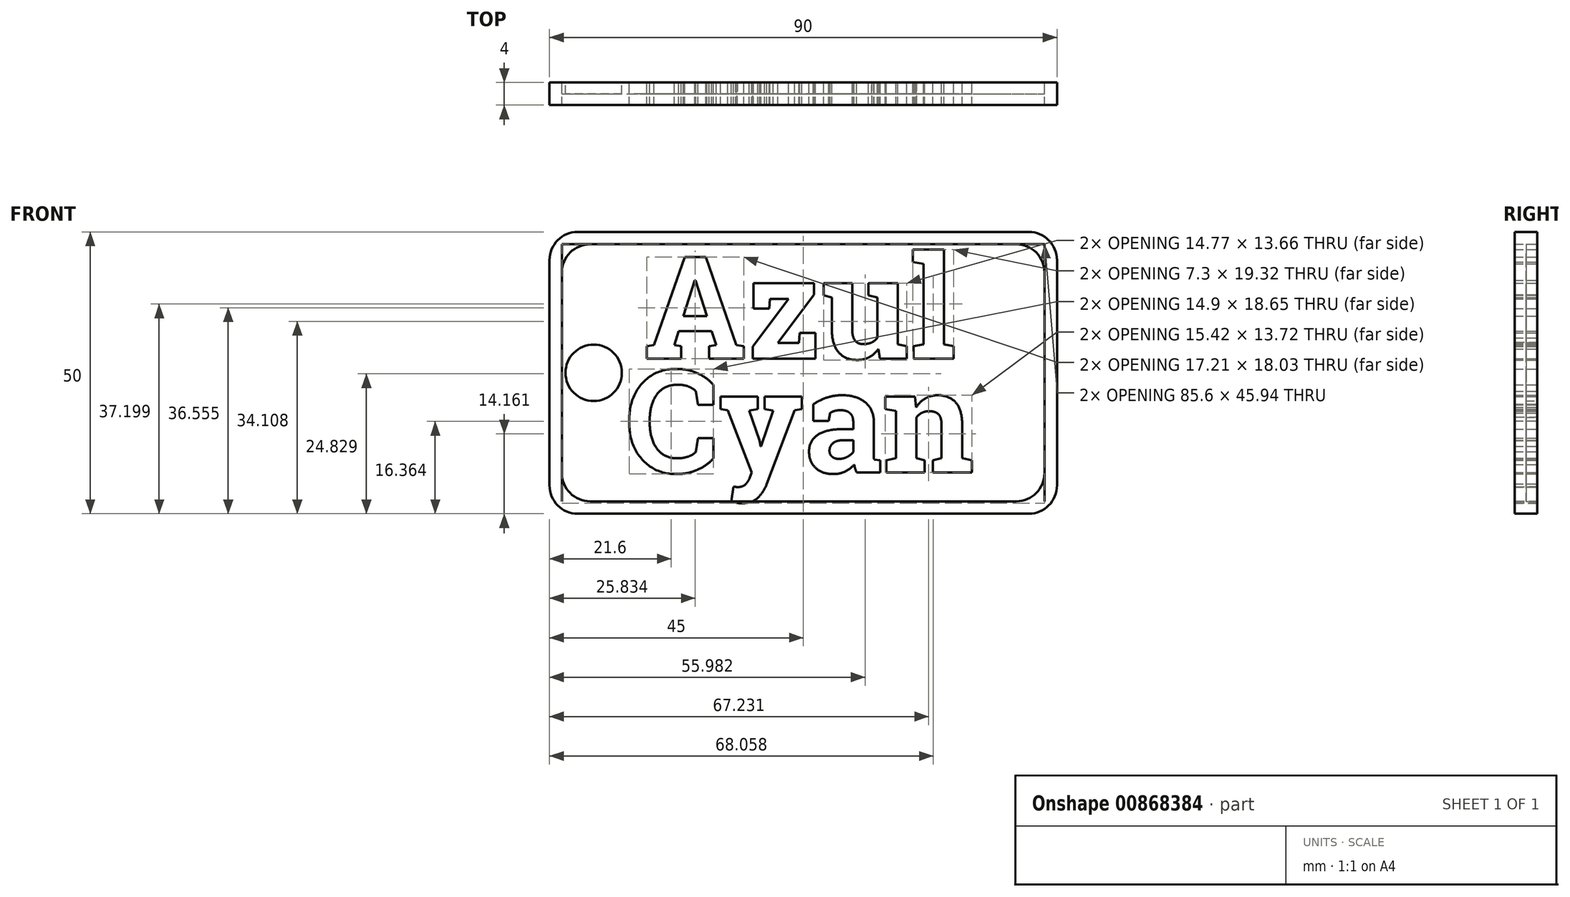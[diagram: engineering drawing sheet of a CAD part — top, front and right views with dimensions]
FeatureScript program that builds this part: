
annotation { "Feature Type Name" : "Feature", "Feature Type Description" : "" }
export const myFeature = defineFeature(function(context is Context, id is Id, definition is map)
    precondition{}
    {
        {
            var Q0;
            Q0=qCreatedBy(makeId("Front.planeOp"),FACE);
            var sketch = newSketch(context, id + "F0", { "sketchPlane" : qUnion([Q0])});
            skLineSegment(sketch, "E0.bottom", {"start": v(-45, 25) * mm, "end": v(45, 25) * mm});
            skLineSegment(sketch, "E0.top", {"start": v(-45, -25) * mm, "end": v(45, -25) * mm});
            skLineSegment(sketch, "E0.left", {"start": v(-45, 25) * mm, "end": v(-45, -25) * mm});
            skLineSegment(sketch, "E0.right", {"start": v(45, 25) * mm, "end": v(45, -25) * mm});
            skLineSegment(sketch, "E1.0", {"start": v(-42.8, 22.8) * mm, "end": v(42.8, 22.8) * mm});
            skLineSegment(sketch, "E1.1", {"start": v(-42.8, 22.8) * mm, "end": v(-42.8, -22.8) * mm});
            skLineSegment(sketch, "E1.2", {"start": v(-42.8, -22.8) * mm, "end": v(42.8, -22.8) * mm});
            skLineSegment(sketch, "E1.3", {"start": v(42.8, 22.8) * mm, "end": v(42.8, -22.8) * mm});
            skCircle(sketch, "E2", {"center": v(-37.16, 0) * mm, "radius": 5 * mm});
            skText(sketch, "E3", { "text": "Azul", "fontName": "RobotoSlab-Bold.ttf"});
            skText(sketch, "E4", { "text": "Cyan", "fontName": "RobotoSlab-Bold.ttf"});
            const initialGuessF0  = {"E3": [-0.02828, 0.00254, 1, 0, 0.01826], "E4": [-0.0315, -0.0177, 1, 0, 0.01836]};
            skSetInitialGuess(sketch, initialGuessF0);
            skSolve(sketch);
        }
        {
            var Q0;
            Q0=makeQuery(id+"F0.imprint","IMPRINT",FACE,{"disambiguationData":[TD([[makeQuery(id+"F0.imprint","IMPRINT",EDGE,{"derivedFrom":sQuery(id+"F0.wireOp",EDGE,"ed1831c7-6287-4320-802f-d40747e157da.sketch_text.stroke-16")}),1.0]])]});
            var Q1;
            Q1=makeQuery(id+"F0.imprint","IMPRINT",FACE,{"disambiguationData":[TD([[makeQuery(id+"F0.imprint","IMPRINT",EDGE,{"derivedFrom":sQuery(id+"F0.wireOp",EDGE,"ed1831c7-6287-4320-802f-d40747e157da.sketch_text.stroke-90")}),1.0]])]});
            var Q2;
            Q2=makeQuery(id+"F0.imprint","IMPRINT",FACE,{"disambiguationData":[TD([[makeQuery(id+"F0.imprint","IMPRINT",EDGE,{"derivedFrom":sQuery(id+"F0.wireOp",EDGE,"ed1831c7-6287-4320-802f-d40747e157da.sketch_text.stroke-161")}),1.0]])]});
            var Q3;
            Q3=makeQuery(id+"F0.imprint","IMPRINT",FACE,{"disambiguationData":[TD([[makeQuery(id+"F0.imprint","IMPRINT",EDGE,{"derivedFrom":sQuery(id+"F0.wireOp",EDGE,"ed1831c7-6287-4320-802f-d40747e157da.sketch_text.stroke-281")}),1.0]])]});
            var Q4;
            Q4=makeQuery(id+"F0.imprint","IMPRINT",FACE,{"disambiguationData":[TD([[makeQuery(id+"F0.imprint","IMPRINT",EDGE,{"derivedFrom":sQuery(id+"F0.wireOp",EDGE,"ed1831c7-6287-4320-802f-d40747e157da.sketch_text.stroke-244")}),1.0]])]});
            var Q5;
            Q5=makeQuery(id+"F0.imprint","IMPRINT",FACE,{"disambiguationData":[TD([[makeQuery(id+"F0.imprint","IMPRINT",EDGE,{"derivedFrom":sQuery(id+"F0.wireOp",EDGE,"ed1831c7-6287-4320-802f-d40747e157da.sketch_text.stroke-218")}),1.0]])]});
            var Q6;
            Q6=makeQuery(id+"F0.imprint","IMPRINT",FACE,{"disambiguationData":[TD([[makeQuery(id+"F0.imprint","IMPRINT",EDGE,{"derivedFrom":sQuery(id+"F0.wireOp",EDGE,"E1.0")}),-1.0]])]});
            var Q7;
            Q7=makeQuery(id+"F0.imprint","IMPRINT",FACE,{"disambiguationData":[TD([[makeQuery(id+"F0.imprint","IMPRINT",EDGE,{"derivedFrom":sQuery(id+"F0.wireOp",EDGE,"E3.sketch_text.stroke-16")}),1.0]])]});
            var Q8;
            Q8=makeQuery(id+"F0.imprint","IMPRINT",FACE,{"disambiguationData":[TD([[makeQuery(id+"F0.imprint","IMPRINT",EDGE,{"derivedFrom":sQuery(id+"F0.wireOp",EDGE,"E4.sketch_text.stroke-77")}),1.0]])]});
            extrude(context, id + "F1", {"entities" : qUnion([Q0, Q1, Q2, Q3, Q4, Q5, Q6, Q7, Q8]), "depth" : 2 * mm, "offsetDistance" : 25 * mm});
        }
        {
            var Q0;
            Q0=makeQuery(id+"F0.imprint","IMPRINT",FACE,{"disambiguationData":[TD([[makeQuery(id+"F0.imprint","IMPRINT",EDGE,{"derivedFrom":sQuery(id+"F0.wireOp",EDGE,"ed1831c7-6287-4320-802f-d40747e157da.sketch_text.stroke-0")}),-1.0]])]});
            var Q1;
            Q1=makeQuery(id+"F0.imprint","IMPRINT",FACE,{"disambiguationData":[TD([[makeQuery(id+"F0.imprint","IMPRINT",EDGE,{"derivedFrom":sQuery(id+"F0.wireOp",EDGE,"ed1831c7-6287-4320-802f-d40747e157da.sketch_text.stroke-20")}),-1.0]])]});
            var Q2;
            Q2=makeQuery(id+"F0.imprint","IMPRINT",FACE,{"disambiguationData":[TD([[makeQuery(id+"F0.imprint","IMPRINT",EDGE,{"derivedFrom":sQuery(id+"F0.wireOp",EDGE,"ed1831c7-6287-4320-802f-d40747e157da.sketch_text.stroke-63")}),-1.0]])]});
            var Q3;
            Q3=makeQuery(id+"F0.imprint","IMPRINT",FACE,{"disambiguationData":[TD([[makeQuery(id+"F0.imprint","IMPRINT",EDGE,{"derivedFrom":sQuery(id+"F0.wireOp",EDGE,"ed1831c7-6287-4320-802f-d40747e157da.sketch_text.stroke-98")}),-1.0]])]});
            var Q4;
            Q4=makeQuery(id+"F0.imprint","IMPRINT",FACE,{"disambiguationData":[TD([[makeQuery(id+"F0.imprint","IMPRINT",EDGE,{"derivedFrom":sQuery(id+"F0.wireOp",EDGE,"ed1831c7-6287-4320-802f-d40747e157da.sketch_text.stroke-117")}),-1.0]])]});
            var Q5;
            Q5=makeQuery(id+"F0.imprint","IMPRINT",FACE,{"disambiguationData":[TD([[makeQuery(id+"F0.imprint","IMPRINT",EDGE,{"derivedFrom":sQuery(id+"F0.wireOp",EDGE,"ed1831c7-6287-4320-802f-d40747e157da.sketch_text.stroke-127")}),-1.0]])]});
            var Q6;
            Q6=makeQuery(id+"F0.imprint","IMPRINT",FACE,{"disambiguationData":[TD([[makeQuery(id+"F0.imprint","IMPRINT",EDGE,{"derivedFrom":sQuery(id+"F0.wireOp",EDGE,"ed1831c7-6287-4320-802f-d40747e157da.sketch_text.stroke-131")}),-1.0]])]});
            var Q7;
            Q7=makeQuery(id+"F0.imprint","IMPRINT",FACE,{"disambiguationData":[TD([[makeQuery(id+"F0.imprint","IMPRINT",EDGE,{"derivedFrom":sQuery(id+"F0.wireOp",EDGE,"ed1831c7-6287-4320-802f-d40747e157da.sketch_text.stroke-141")}),-1.0]])]});
            var Q8;
            Q8=makeQuery(id+"F0.imprint","IMPRINT",FACE,{"disambiguationData":[TD([[makeQuery(id+"F0.imprint","IMPRINT",EDGE,{"derivedFrom":sQuery(id+"F0.wireOp",EDGE,"ed1831c7-6287-4320-802f-d40747e157da.sketch_text.stroke-151")}),-1.0]])]});
            var Q9;
            Q9=makeQuery(id+"F0.imprint","IMPRINT",FACE,{"disambiguationData":[TD([[makeQuery(id+"F0.imprint","IMPRINT",EDGE,{"derivedFrom":sQuery(id+"F0.wireOp",EDGE,"ed1831c7-6287-4320-802f-d40747e157da.sketch_text.stroke-254")}),-1.0]])]});
            var Q10;
            Q10=makeQuery(id+"F0.imprint","IMPRINT",FACE,{"disambiguationData":[TD([[makeQuery(id+"F0.imprint","IMPRINT",EDGE,{"derivedFrom":sQuery(id+"F0.wireOp",EDGE,"ed1831c7-6287-4320-802f-d40747e157da.sketch_text.stroke-225")}),-1.0]])]});
            var Q11;
            Q11=makeQuery(id+"F0.imprint","IMPRINT",FACE,{"disambiguationData":[TD([[makeQuery(id+"F0.imprint","IMPRINT",EDGE,{"derivedFrom":sQuery(id+"F0.wireOp",EDGE,"ed1831c7-6287-4320-802f-d40747e157da.sketch_text.stroke-201")}),-1.0]])]});
            var Q12;
            Q12=makeQuery(id+"F0.imprint","IMPRINT",FACE,{"disambiguationData":[TD([[makeQuery(id+"F0.imprint","IMPRINT",EDGE,{"derivedFrom":sQuery(id+"F0.wireOp",EDGE,"ed1831c7-6287-4320-802f-d40747e157da.sketch_text.stroke-171")}),-1.0]])]});
            var Q13;
            Q13=makeQuery(id+"F0.imprint","IMPRINT",FACE,{"disambiguationData":[TD([[makeQuery(id+"F0.imprint","IMPRINT",EDGE,{"derivedFrom":sQuery(id+"F0.wireOp",EDGE,"E0.bottom")}),-1.0]])]});
            var Q14;
            Q14=makeQuery(id+"F0.imprint","IMPRINT",FACE,{"disambiguationData":[TD([[makeQuery(id+"F0.imprint","IMPRINT",EDGE,{"derivedFrom":sQuery(id+"F0.wireOp",EDGE,"E3.sketch_text.stroke-0")}),-1.0]])]});
            var Q15;
            Q15=makeQuery(id+"F0.imprint","IMPRINT",FACE,{"disambiguationData":[TD([[makeQuery(id+"F0.imprint","IMPRINT",EDGE,{"derivedFrom":sQuery(id+"F0.wireOp",EDGE,"E3.sketch_text.stroke-20")}),-1.0]])]});
            var Q16;
            Q16=makeQuery(id+"F0.imprint","IMPRINT",FACE,{"disambiguationData":[TD([[makeQuery(id+"F0.imprint","IMPRINT",EDGE,{"derivedFrom":sQuery(id+"F0.wireOp",EDGE,"E3.sketch_text.stroke-34")}),-1.0]])]});
            var Q17;
            Q17=makeQuery(id+"F0.imprint","IMPRINT",FACE,{"disambiguationData":[TD([[makeQuery(id+"F0.imprint","IMPRINT",EDGE,{"derivedFrom":sQuery(id+"F0.wireOp",EDGE,"E3.sketch_text.stroke-58")}),-1.0]])]});
            var Q18;
            Q18=makeQuery(id+"F0.imprint","IMPRINT",FACE,{"disambiguationData":[TD([[makeQuery(id+"F0.imprint","IMPRINT",EDGE,{"derivedFrom":sQuery(id+"F0.wireOp",EDGE,"E4.sketch_text.stroke-85")}),-1.0]])]});
            var Q19;
            Q19=makeQuery(id+"F0.imprint","IMPRINT",FACE,{"disambiguationData":[TD([[makeQuery(id+"F0.imprint","IMPRINT",EDGE,{"derivedFrom":sQuery(id+"F0.wireOp",EDGE,"E4.sketch_text.stroke-50")}),-1.0]])]});
            var Q20;
            Q20=makeQuery(id+"F0.imprint","IMPRINT",FACE,{"disambiguationData":[TD([[makeQuery(id+"F0.imprint","IMPRINT",EDGE,{"derivedFrom":sQuery(id+"F0.wireOp",EDGE,"E4.sketch_text.stroke-24")}),-1.0]])]});
            var Q21;
            Q21=makeQuery(id+"F0.imprint","IMPRINT",FACE,{"disambiguationData":[TD([[makeQuery(id+"F0.imprint","IMPRINT",EDGE,{"derivedFrom":sQuery(id+"F0.wireOp",EDGE,"E4.sketch_text.stroke-0")}),-1.0]])]});
            extrude(context, id + "F2", {"entities" : qUnion([Q0, Q1, Q2, Q3, Q4, Q5, Q6, Q7, Q8, Q9, Q10, Q11, Q12, Q13, Q14, Q15, Q16, Q17, Q18, Q19, Q20, Q21]), "depth" : 4 * mm, "offsetDistance" : 25 * mm});
        }
        {
            var Q0;
            Q0=makeQuery(id+"F2.opExtrude","SWEPT_EDGE",EDGE,{"disambiguationData":[OSD([sQuery(id+"F0.wireOp",EDGE,"E0.top"),sQuery(id+"F0.wireOp",EDGE,"E0.left")])]});
            var Q1;
            Q1=makeQuery(id+"F2.opExtrude","SWEPT_EDGE",EDGE,{"disambiguationData":[OSD([sQuery(id+"F0.wireOp",EDGE,"E0.bottom"),sQuery(id+"F0.wireOp",EDGE,"E0.left")])]});
            var Q2;
            Q2=makeQuery(id+"F2.opExtrude","SWEPT_EDGE",EDGE,{"disambiguationData":[OSD([sQuery(id+"F0.wireOp",EDGE,"E1.1"),sQuery(id+"F0.wireOp",EDGE,"E1.2")])]});
            var Q3;
            Q3=makeQuery(id+"F2.opExtrude","SWEPT_EDGE",EDGE,{"disambiguationData":[OSD([sQuery(id+"F0.wireOp",EDGE,"E1.0"),sQuery(id+"F0.wireOp",EDGE,"E1.1")])]});
            var Q4;
            Q4=makeQuery(id+"F2.opExtrude","SWEPT_EDGE",EDGE,{"disambiguationData":[OSD([sQuery(id+"F0.wireOp",EDGE,"E1.0"),sQuery(id+"F0.wireOp",EDGE,"E1.3")])]});
            var Q5;
            Q5=makeQuery(id+"F2.opExtrude","SWEPT_EDGE",EDGE,{"disambiguationData":[OSD([sQuery(id+"F0.wireOp",EDGE,"E1.2"),sQuery(id+"F0.wireOp",EDGE,"E1.3")])]});
            var Q6;
            Q6=makeQuery(id+"F2.opExtrude","SWEPT_EDGE",EDGE,{"disambiguationData":[OSD([sQuery(id+"F0.wireOp",EDGE,"E0.top"),sQuery(id+"F0.wireOp",EDGE,"E0.right")])]});
            var Q7;
            Q7=makeQuery(id+"F2.opExtrude","SWEPT_EDGE",EDGE,{"disambiguationData":[OSD([sQuery(id+"F0.wireOp",EDGE,"E0.bottom"),sQuery(id+"F0.wireOp",EDGE,"E0.right")])]});
            fillet(context, id + "F3", {"entities" : qUnion([Q0, Q1, Q2, Q3, Q4, Q5, Q6, Q7]), "radius" : 5 * mm, "tangentPropagation" : true, "allowEdgeOverflow" : false});
        }
    });
